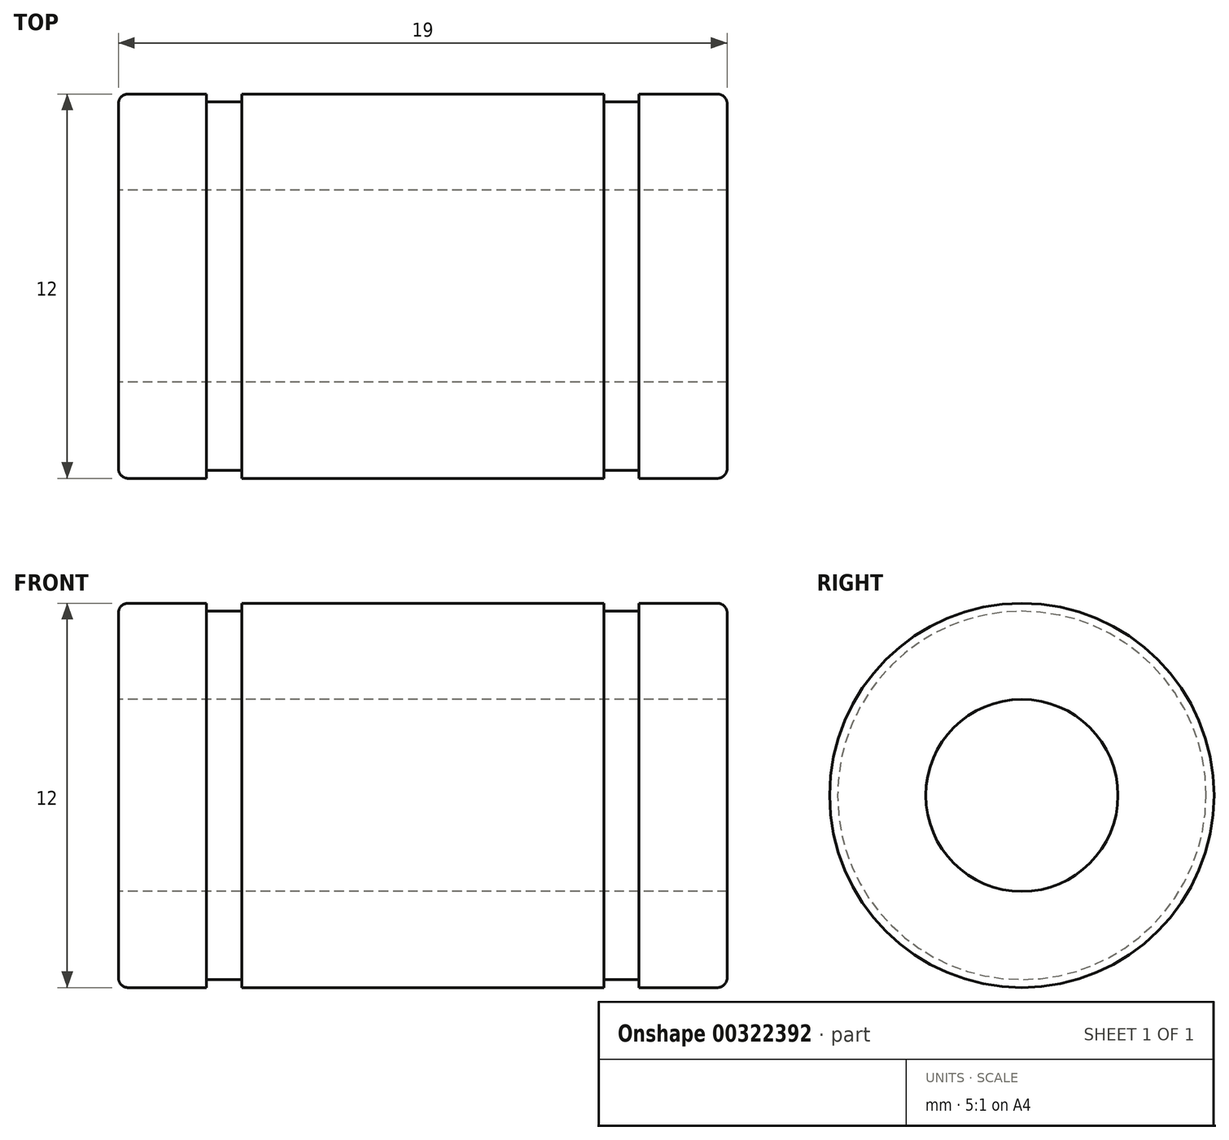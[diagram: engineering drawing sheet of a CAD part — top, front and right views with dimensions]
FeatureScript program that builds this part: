
annotation { "Feature Type Name" : "Feature", "Feature Type Description" : "" }
export const myFeature = defineFeature(function(context is Context, id is Id, definition is map)
    precondition{}
    {
        {
            assignVariable(context, id + "F0", {"name" : "D", "anyValue" : 12 * mm});
        }
        {
            var Q0;
            Q0=qCreatedBy(makeId("Front.planeOp"),FACE);
            var sketch = newSketch(context, id + "F1", { "sketchPlane" : qUnion([Q0])});
            skLineSegment(sketch, "E0", {"start": v(-9.5, 0) * mm, "end": v(9.5, 0) * mm, "construction": true});
            skLineSegment(sketch, "E1", {"start": v(-9.5, 3) * mm, "end": v(9.5, 3) * mm});
            skLineSegment(sketch, "E2", {"start": v(9.5, 3) * mm, "end": v(9.5, 6) * mm});
            skLineSegment(sketch, "E3", {"start": v(9.5, 6) * mm, "end": v(6.75, 6) * mm});
            skLineSegment(sketch, "E4", {"start": v(6.75, 6) * mm, "end": v(6.75, 5.75) * mm});
            skLineSegment(sketch, "E5", {"start": v(6.75, 5.75) * mm, "end": v(5.65, 5.75) * mm});
            skLineSegment(sketch, "E6", {"start": v(5.65, 5.75) * mm, "end": v(5.65, 6) * mm});
            skLineSegment(sketch, "E7", {"start": v(5.65, 6) * mm, "end": v(-5.65, 6) * mm});
            skLineSegment(sketch, "E8", {"start": v(-5.65, 6) * mm, "end": v(-5.65, 5.75) * mm});
            skLineSegment(sketch, "E9", {"start": v(-5.65, 5.75) * mm, "end": v(-6.75, 5.75) * mm});
            skLineSegment(sketch, "E10", {"start": v(-6.75, 5.75) * mm, "end": v(-6.75, 6) * mm});
            skLineSegment(sketch, "E11", {"start": v(-6.75, 6) * mm, "end": v(-9.5, 6) * mm});
            skLineSegment(sketch, "E12", {"start": v(-9.5, 6) * mm, "end": v(-9.5, 3) * mm});
            skSolve(sketch);
        }
        {
            var Q0;
            Q0 = qSketchRegion(id + "F1", true);
            var Q1;
            Q1=sQuery(id+"F1.wireOp",EDGE,"E0");
            revolve(context, id + "F2", {"entities" : qUnion([Q0]), "axis" : qUnion([Q1]), "revolveType" : RevolveType.FULL});
        }
        {
            var Q0;
            Q0=makeQuery(id+"F2.opRevolve","SWEPT_EDGE",EDGE,{"disambiguationData":[OSD([sQuery(id+"F1.wireOp",EDGE,"E11"),sQuery(id+"F1.wireOp",EDGE,"E12")])]});
            var Q1;
            Q1=makeQuery(id+"F2.opRevolve","SWEPT_EDGE",EDGE,{"disambiguationData":[OSD([sQuery(id+"F1.wireOp",EDGE,"E2"),sQuery(id+"F1.wireOp",EDGE,"E3")])]});
            fillet(context, id + "F3", {"entities" : qUnion([Q0, Q1]), "radius" : getVariable(context, 'D') * 0.03, "tangentPropagation" : true, "allowEdgeOverflow" : false});
        }
    });
